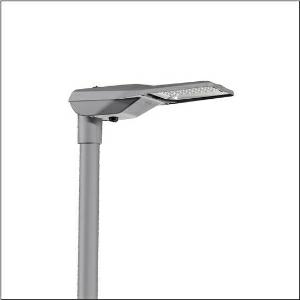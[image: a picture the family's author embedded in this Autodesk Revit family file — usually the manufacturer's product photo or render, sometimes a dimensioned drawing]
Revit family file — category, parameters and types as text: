
# Revit family: streetlight_sl_21_mini___p1_0a_5xe2a43t08gb_2ff8
name_source: partatom
category: Lighting Fixtures
units: mm (PartAtom-declared; Revit-internal decimal feet)

## family parameters
Cut with Voids When Loaded = No
Host = Face
Light Source = No
Part Type = Normal
Room Calculation Point = No
Round Connector Dimension = Use Diameter
Shared = No

## types (1)
- --- (1 x LED, 6180 lm, 40.4 W, 4000K)
    Apparent Load = 40 VA
    CIE Flux Codes = 21 50 90 100 100
    Color Rendering = 70
    Color Temperature = 4000K
    Default Elevation = 1800 mm
    Description = Streetlight SL 21 mini, mast luminaire, primary light control with lens, of PMMA, primary optical cover: cover, of toughened safety glass, transparent, light distribution: P1.0a, light emission: direct distribution, primary light characteristic: asymmetric, installation type: side-entry, post-top, LED, High Power LED, rated luminous flux: 6.180lm, luminous efficacy: 153lm/W, light colour: 740, colour temperature: 4000K, control gear: D4i, control: overheat protection, constant luminous flux control, time-dependent luminous flux control, flexible luminous flux parameterisation, pre-setting: logarithmic dimming characteristic, mains connection: 220..240V, AC, 50/60Hz, start of lifetime: 40W, end of service life: 41W, reduction: 19W, luminaire housing, of diecast aluminium, powder-coated, SITECO metallic grey (DB 702S), corrosivity category C5 high according to DIN EN ISO 12944, please order mast flange separately, inclination adjustable: 0°, 5°, 10°, 15°, sealing non-destructively replaceable, multi-level sealing system, length: 628mm, width: 235mm, height: 110mm, mast flange for spigot size: 42mm (side-entry): 5XC10008XM4, 60/48mm (side-entry/post-top): 5XC10108XM2, 76/60mm (side-entry/post-top): 5XC10108XM1, mounting height: 4..8m, Smart Interface below and above, protection rating (complete): IP66, insulation class (complete): insulation class II (safety insulation), certification: CE, ENEC, ENEC+, VDE, impact resistance: IK10, permissible operating ambient temperature for outdoor applications: -40..+50°C, standard-compliant lighting for roads and squares, packaging unit: 1 piece

Light Distribution: P1.0a
    Height = 110 mm
    Lamp = 1 x LED
    Lamp Light Flux = 6180 lm
    Lamp Power = 40.4 W
    Lamp count = 1
    Length = 625 mm
    Luminous efficacy = 153 lm/W
    Manufacturer = Siteco
    ModVariant = No
    Model = 5XE2A43T08GB
    Number of Poles = 1
    OnlyDefault = Yes
    Power Factor = 1
    Product Name = Streetlight SL 21 mini | P1.0a
    Product group = mast luminaire | pylon top
    ProductGroupID = 6100
    Protection Class = Protection class II
    Protection Degree = IP 66
    RLX_Detail_Level = 1
    RLX_Emergency_Light_Flux = 0 lm
    RLX_Emergency_Type = 0
    RLX_Emergency_Type_DB = No
    RlxData = <blob elided: 37541 chars, md5=e2cbfd14>
    Socket = socket
    Standby Power = 0 W
    System Light Flux = 6180 lm
    System Power = 40 W
    Type Comments = factory setting: luminous flux: 100 % | dim-lin: 254 | 812 mA
    Type Image = l_1003514.jpg
    URL = http://relux.com
    VarID = @adj_183979
    Voltage = 0 V
    Weight = 0.00 kg
    Width = 234 mm

## geometry (parser evidence)
native form markers: Blend x4, Sweep x11
no freeform markers — native parametric forms only
